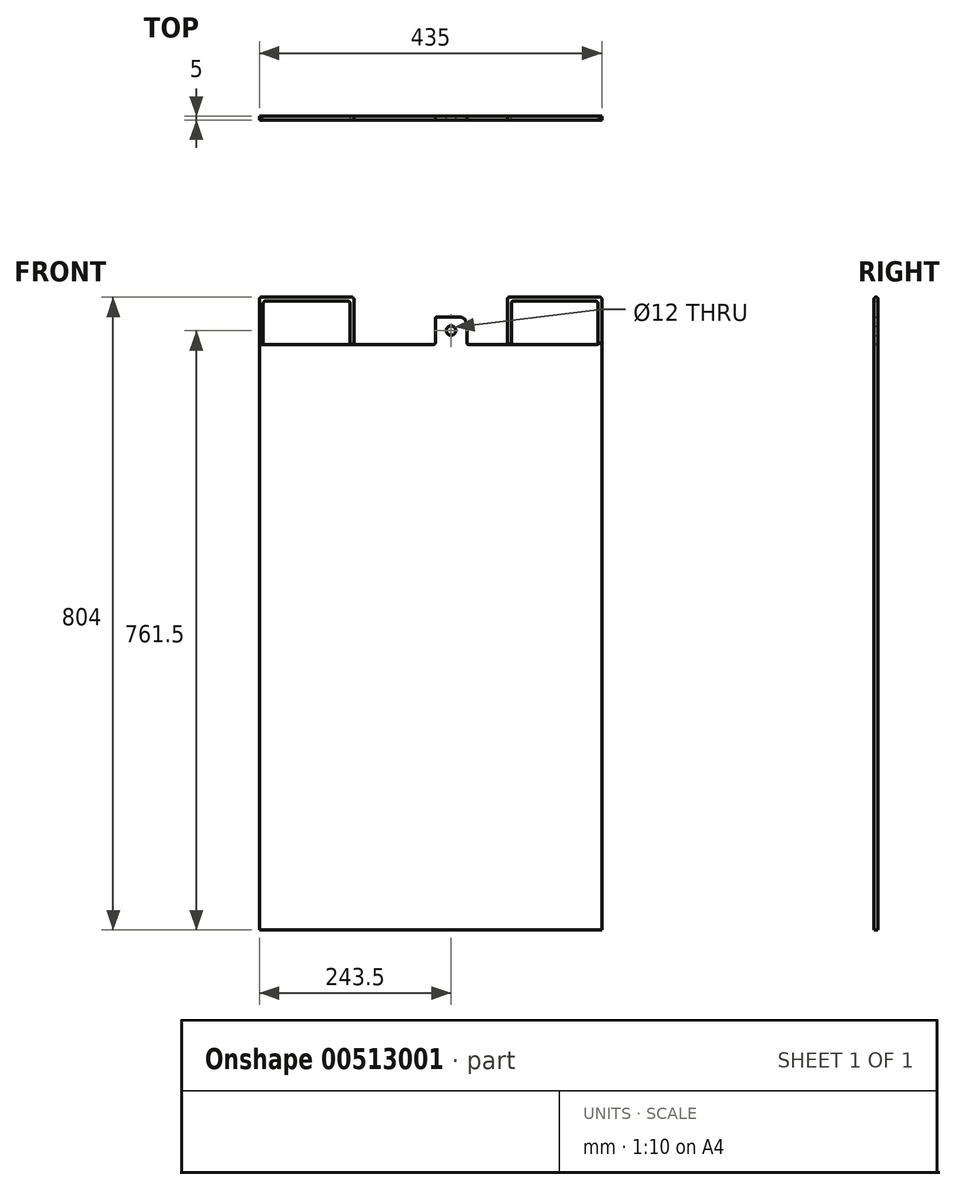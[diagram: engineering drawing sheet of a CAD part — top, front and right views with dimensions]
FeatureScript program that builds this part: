
annotation { "Feature Type Name" : "Feature", "Feature Type Description" : "" }
export const myFeature = defineFeature(function(context is Context, id is Id, definition is map)
    precondition{}
    {
        {
            var Q0;
            Q0=qCreatedBy(makeId("Front.planeOp"),FACE);
            var sketch = newSketch(context, id + "F0", { "sketchPlane" : qUnion([Q0])});
            skLineSegment(sketch, "E0.bottom", {"start": v(217.5, 372) * mm, "end": v(-217.5, 372) * mm});
            skLineSegment(sketch, "E0.top", {"start": v(217.5, -372) * mm, "end": v(-217.5, -372) * mm});
            skLineSegment(sketch, "E0.left", {"start": v(217.5, 372) * mm, "end": v(217.5, -372) * mm});
            skLineSegment(sketch, "E0.right", {"start": v(-217.5, 372) * mm, "end": v(-217.5, -372) * mm});
            skPoint(sketch, "E0.middle", {"position": v(0, 0) * mm});
            skLineSegment(sketch, "E1.bottom", {"start": v(6, 372) * mm, "end": v(46, 372) * mm});
            skLineSegment(sketch, "E1.top", {"start": v(6, 407) * mm, "end": v(46, 407) * mm});
            skLineSegment(sketch, "E1.left", {"start": v(6, 372) * mm, "end": v(6, 407) * mm});
            skLineSegment(sketch, "E1.right", {"start": v(46, 372) * mm, "end": v(46, 407) * mm});
            skPoint(sketch, "E2", {"position": v(0, 372) * mm});
            skLineSegment(sketch, "E3", {"start": v(0, -372) * mm, "end": v(0, 372) * mm, "construction": true});
            skLineSegment(sketch, "E4.bottom", {"start": v(-217.5, 372) * mm, "end": v(-97.5, 372) * mm});
            skLineSegment(sketch, "E4.top", {"start": v(-217.5, 432) * mm, "end": v(-97.5, 432) * mm});
            skLineSegment(sketch, "E4.left", {"start": v(-217.5, 372) * mm, "end": v(-217.5, 432) * mm});
            skLineSegment(sketch, "E4.right", {"start": v(-97.5, 372) * mm, "end": v(-97.5, 432) * mm});
            skPoint(sketch, "E5", {"position": v(26, 389.5) * mm});
            skPoint(sketch, "E5.positionSnap0", {"position": v(26, 372) * mm});
            skPoint(sketch, "E5.positionSnap1", {"position": v(46, 389.5) * mm});
            skLineSegment(sketch, "E6.0", {"start": v(-102.5, 372) * mm, "end": v(-102.5, 427) * mm});
            skLineSegment(sketch, "E6.1", {"start": v(-212.5, 427) * mm, "end": v(-102.5, 427) * mm});
            skLineSegment(sketch, "E6.2", {"start": v(-212.5, 372) * mm, "end": v(-212.5, 427) * mm});
            skLineSegment(sketch, "E7.MirrorCS", {"start": v(97.5, 372) * mm, "end": v(97.5, 432) * mm});
            skLineSegment(sketch, "E8.MirrorCS", {"start": v(102.5, 372) * mm, "end": v(102.5, 427) * mm});
            skLineSegment(sketch, "E9.MirrorCS", {"start": v(212.5, 427) * mm, "end": v(102.5, 427) * mm});
            skLineSegment(sketch, "E10.MirrorCS", {"start": v(217.5, 432) * mm, "end": v(97.5, 432) * mm});
            skLineSegment(sketch, "E11.MirrorCS", {"start": v(212.5, 372) * mm, "end": v(212.5, 427) * mm});
            skLineSegment(sketch, "E12.MirrorCS", {"start": v(217.5, 372) * mm, "end": v(217.5, 432) * mm});
            skSolve(sketch);
        }
        {
            var Q0;
            Q0 = qSketchRegion(id + "F0", true);
            extrude(context, id + "F1", {"entities" : qUnion([Q0]), "depth" : 5 * mm});
        }
        {
            var Q0;
            Q0=sQuery(id+"F0.wireOp",VERTEX,"E5");
            var Q1;
            Q1=makeQuery(id+"F1.opExtrude","SWEPT_BODY",BODY,{"disambiguationData":[OSD([sQuery(id+"F0.wireOp",EDGE,"E0.bottom"),sQuery(id+"F0.wireOp",EDGE,"E0.top"),sQuery(id+"F0.wireOp",EDGE,"E0.left"),sQuery(id+"F0.wireOp",EDGE,"E0.right"),sQuery(id+"F0.wireOp",EDGE,"E1.top"),sQuery(id+"F0.wireOp",EDGE,"E1.left"),sQuery(id+"F0.wireOp",EDGE,"E1.right"),sQuery(id+"F0.wireOp",EDGE,"E4.bottom"),sQuery(id+"F0.wireOp",EDGE,"E4.top"),sQuery(id+"F0.wireOp",EDGE,"E4.left"),sQuery(id+"F0.wireOp",EDGE,"E4.right"),sQuery(id+"F0.wireOp",EDGE,"E6.0"),sQuery(id+"F0.wireOp",EDGE,"E6.1"),sQuery(id+"F0.wireOp",EDGE,"E6.2"),sQuery(id+"F0.wireOp",EDGE,"E7.MirrorCS"),sQuery(id+"F0.wireOp",EDGE,"E8.MirrorCS"),sQuery(id+"F0.wireOp",EDGE,"E9.MirrorCS"),sQuery(id+"F0.wireOp",EDGE,"E10.MirrorCS"),sQuery(id+"F0.wireOp",EDGE,"E11.MirrorCS"),sQuery(id+"F0.wireOp",EDGE,"E12.MirrorCS")])]});
            hole(context, id + "F2", {"style" : HoleStyle.SIMPLE, "endStyle" : HoleEndStyle.THROUGH, "oppositeDirection" : true, "holeDiameter" : 12 * mm, "tappedDepth" : 12 * mm, "tapClearance" : 3, "locations" : qUnion([Q0]), "scope" : qUnion([Q1])});
        }
        {
            var Q0;
            Q0=makeQuery(id+"F1.opExtrude","SWEPT_EDGE",EDGE,{"disambiguationData":[OSD([sQuery(id+"F0.wireOp",EDGE,"E1.top"),sQuery(id+"F0.wireOp",EDGE,"E1.right")])]});
            fillet(context, id + "F3", {"entities" : qUnion([Q0]), "radius" : 10 * mm, "tangentPropagation" : true, "allowEdgeOverflow" : false});
        }
        {
            var Q0;
            Q0=makeQuery(id+"F1.opExtrude","CAP_EDGE",EDGE,{"disambiguationData":[OSD([sQuery(id+"F0.wireOp",EDGE,"E4.top")])],"isStart":true});
            var Q1;
            Q1=makeQuery(id+"F1.opExtrude","CAP_EDGE",EDGE,{"disambiguationData":[OSD([sQuery(id+"F0.wireOp",EDGE,"E4.top")])],"isStart":false});
            var Q2;
            Q2=makeQuery(id+"F1.opExtrude","CAP_EDGE",EDGE,{"disambiguationData":[OSD([sQuery(id+"F0.wireOp",EDGE,"E6.2")])],"isStart":false});
            var Q3;
            Q3=makeQuery(id+"F1.opExtrude","CAP_EDGE",EDGE,{"disambiguationData":[OSD([sQuery(id+"F0.wireOp",EDGE,"E6.2")])],"isStart":true});
            var Q4;
            Q4=makeQuery(id+"F1.opExtrude","CAP_EDGE",EDGE,{"disambiguationData":[OSD([sQuery(id+"F0.wireOp",EDGE,"E6.1")])],"isStart":false});
            var Q5;
            Q5=makeQuery(id+"F1.opExtrude","CAP_EDGE",EDGE,{"disambiguationData":[OSD([sQuery(id+"F0.wireOp",EDGE,"E6.1")])],"isStart":true});
            var Q6;
            Q6=makeQuery(id+"F1.opExtrude","CAP_EDGE",EDGE,{"disambiguationData":[OSD([sQuery(id+"F0.wireOp",EDGE,"E6.0")])],"isStart":false});
            var Q7;
            Q7=makeQuery(id+"F1.opExtrude","CAP_EDGE",EDGE,{"disambiguationData":[OSD([sQuery(id+"F0.wireOp",EDGE,"E6.0")])],"isStart":true});
            var Q8;
            Q8=makeQuery(id+"F1.opExtrude","CAP_EDGE",EDGE,{"disambiguationData":[OSD([sQuery(id+"F0.wireOp",EDGE,"E4.right")])],"isStart":false});
            var Q9;
            Q9=makeQuery(id+"F1.opExtrude","CAP_EDGE",EDGE,{"disambiguationData":[OSD([sQuery(id+"F0.wireOp",EDGE,"E4.right")])],"isStart":true});
            var Q10;
            Q10=makeQuery(id+"F1.opExtrude","SWEPT_EDGE",EDGE,{"disambiguationData":[OSD([sQuery(id+"F0.wireOp",EDGE,"E4.top"),sQuery(id+"F0.wireOp",EDGE,"E4.right")])]});
            var Q11;
            Q11=makeQuery(id+"F1.opExtrude","SWEPT_EDGE",EDGE,{"disambiguationData":[OSD([sQuery(id+"F0.wireOp",EDGE,"E4.top"),sQuery(id+"F0.wireOp",EDGE,"E4.left")])]});
            var Q12;
            Q12=makeQuery(id+"F1.opExtrude","SWEPT_EDGE",EDGE,{"disambiguationData":[OSD([sQuery(id+"F0.wireOp",EDGE,"E6.0"),sQuery(id+"F0.wireOp",EDGE,"E6.1")])]});
            var Q13;
            Q13=makeQuery(id+"F1.opExtrude","SWEPT_EDGE",EDGE,{"disambiguationData":[OSD([sQuery(id+"F0.wireOp",EDGE,"E6.1"),sQuery(id+"F0.wireOp",EDGE,"E6.2")])]});
            var Q14;
            Q14=makeQuery(id+"F1.opExtrude","CAP_EDGE",EDGE,{"disambiguationData":[OSD([sQuery(id+"F0.wireOp",EDGE,"E8.MirrorCS")])],"isStart":false});
            var Q15;
            Q15=makeQuery(id+"F1.opExtrude","CAP_EDGE",EDGE,{"disambiguationData":[OSD([sQuery(id+"F0.wireOp",EDGE,"E8.MirrorCS")])],"isStart":true});
            var Q16;
            Q16=makeQuery(id+"F1.opExtrude","CAP_EDGE",EDGE,{"disambiguationData":[OSD([sQuery(id+"F0.wireOp",EDGE,"E9.MirrorCS")])],"isStart":false});
            var Q17;
            Q17=makeQuery(id+"F1.opExtrude","CAP_EDGE",EDGE,{"disambiguationData":[OSD([sQuery(id+"F0.wireOp",EDGE,"E10.MirrorCS")])],"isStart":false});
            var Q18;
            Q18=makeQuery(id+"F1.opExtrude","CAP_EDGE",EDGE,{"disambiguationData":[OSD([sQuery(id+"F0.wireOp",EDGE,"E10.MirrorCS")])],"isStart":true});
            var Q19;
            Q19=makeQuery(id+"F1.opExtrude","CAP_EDGE",EDGE,{"disambiguationData":[OSD([sQuery(id+"F0.wireOp",EDGE,"E7.MirrorCS")])],"isStart":false});
            var Q20;
            Q20=makeQuery(id+"F1.opExtrude","CAP_EDGE",EDGE,{"disambiguationData":[OSD([sQuery(id+"F0.wireOp",EDGE,"E11.MirrorCS")])],"isStart":false});
            var Q21;
            Q21=makeQuery(id+"F1.opExtrude","CAP_EDGE",EDGE,{"disambiguationData":[OSD([sQuery(id+"F0.wireOp",EDGE,"E11.MirrorCS")])],"isStart":true});
            var Q22;
            Q22=makeQuery(id+"F1.opExtrude","CAP_EDGE",EDGE,{"disambiguationData":[OSD([sQuery(id+"F0.wireOp",EDGE,"E9.MirrorCS")])],"isStart":true});
            var Q23;
            Q23=makeQuery(id+"F1.opExtrude","SWEPT_EDGE",EDGE,{"disambiguationData":[OSD([sQuery(id+"F0.wireOp",EDGE,"E10.MirrorCS"),sQuery(id+"F0.wireOp",EDGE,"E12.MirrorCS")])]});
            var Q24;
            Q24=makeQuery(id+"F1.opExtrude","SWEPT_EDGE",EDGE,{"disambiguationData":[OSD([sQuery(id+"F0.wireOp",EDGE,"E7.MirrorCS"),sQuery(id+"F0.wireOp",EDGE,"E10.MirrorCS")])]});
            var Q25;
            Q25=makeQuery(id+"F1.opExtrude","CAP_EDGE",EDGE,{"disambiguationData":[OSD([sQuery(id+"F0.wireOp",EDGE,"E7.MirrorCS")])],"isStart":true});
            var Q26;
            Q26=makeQuery(id+"F1.opExtrude","SWEPT_EDGE",EDGE,{"disambiguationData":[OSD([sQuery(id+"F0.wireOp",EDGE,"E8.MirrorCS"),sQuery(id+"F0.wireOp",EDGE,"E9.MirrorCS")])]});
            var Q27;
            Q27=makeQuery(id+"F1.opExtrude","SWEPT_EDGE",EDGE,{"disambiguationData":[OSD([sQuery(id+"F0.wireOp",EDGE,"E9.MirrorCS"),sQuery(id+"F0.wireOp",EDGE,"E11.MirrorCS")])]});
            fillet(context, id + "F4", {"entities" : qUnion([Q0, Q1, Q2, Q3, Q4, Q5, Q6, Q7, Q8, Q9, Q10, Q11, Q12, Q13, Q14, Q15, Q16, Q17, Q18, Q19, Q20, Q21, Q22, Q23, Q24, Q25, Q26, Q27]), "radius" : 2.5 * mm, "tangentPropagation" : true, "allowEdgeOverflow" : false});
        }
        {
            var Q0;
            {var subQ0=sQuery(id+"F0.wireOp",EDGE,"E4.right");var subQ1=sQuery(id+"F0.wireOp",EDGE,"E0.bottom");Q0=makeQuery(id+"F4.opFillet","BLEND_EDGE",EDGE,{"blendedFrom":[makeQuery(id+"F1.opExtrude","CAP_EDGE",EDGE,{"disambiguationData":[OSD([subQ0])],"isStart":true}),makeQuery(id+"F1.opExtrude","SWEPT_FACE",FACE,{"disambiguationData":[OSD([subQ1]),TDD([makeQuery(id+"F0.imprint","IMPRINT",EDGE,{"disambiguationData":[TD([[makeQuery(id+"F0.imprint","INTERSECT",VERTEX,{"derivedFrom":[subQ1,sQuery(id+"F0.wireOp",EDGE,"E4.bottom"),subQ0]}),1.0]])],"derivedFrom":subQ1})])]})],"blendedInto":[makeQuery(id+"F1.opExtrude","SWEPT_FACE",FACE,{"disambiguationData":[OSD([subQ1]),TDD([makeQuery(id+"F0.imprint","IMPRINT",EDGE,{"disambiguationData":[TD([[makeQuery(id+"F0.imprint","INTERSECT",VERTEX,{"derivedFrom":[subQ1,sQuery(id+"F0.wireOp",EDGE,"E4.bottom"),subQ0]}),1.0]])],"derivedFrom":subQ1})])]})]});}
            var Q1;
            Q1=makeQuery(id+"F4.opFillet","BLEND_EDGE",EDGE,{"blendedFrom":[makeQuery(id+"F1.opExtrude","CAP_EDGE",EDGE,{"disambiguationData":[OSD([sQuery(id+"F0.wireOp",EDGE,"E6.2")])],"isStart":true}),makeQuery(id+"F1.opExtrude","SWEPT_FACE",FACE,{"disambiguationData":[OSD([sQuery(id+"F0.wireOp",EDGE,"E4.bottom")])]})],"blendedInto":[makeQuery(id+"F1.opExtrude","SWEPT_FACE",FACE,{"disambiguationData":[OSD([sQuery(id+"F0.wireOp",EDGE,"E4.bottom")])]})]});
            var Q2;
            {var subQ0=sQuery(id+"F0.wireOp",EDGE,"E0.bottom");var subQ1=sQuery(id+"F0.wireOp",EDGE,"E11.MirrorCS");Q2=makeQuery(id+"F4.opFillet","BLEND_EDGE",EDGE,{"blendedFrom":[makeQuery(id+"F1.opExtrude","CAP_EDGE",EDGE,{"disambiguationData":[OSD([subQ1])],"isStart":true}),makeQuery(id+"F1.opExtrude","SWEPT_FACE",FACE,{"disambiguationData":[OSD([subQ0]),TDD([makeQuery(id+"F0.imprint","IMPRINT",EDGE,{"disambiguationData":[TD([[makeQuery(id+"F0.imprint","INTERSECT",VERTEX,{"derivedFrom":[subQ0,sQuery(id+"F0.wireOp",EDGE,"E8.MirrorCS")]}),1.0]])],"derivedFrom":subQ0})])]})],"blendedInto":[makeQuery(id+"F1.opExtrude","SWEPT_FACE",FACE,{"disambiguationData":[OSD([subQ0]),TDD([makeQuery(id+"F0.imprint","IMPRINT",EDGE,{"disambiguationData":[TD([[makeQuery(id+"F0.imprint","INTERSECT",VERTEX,{"derivedFrom":[subQ0,sQuery(id+"F0.wireOp",EDGE,"E8.MirrorCS")]}),1.0]])],"derivedFrom":subQ0})])]})]});}
            var Q3;
            {var subQ0=sQuery(id+"F0.wireOp",EDGE,"E8.MirrorCS");var subQ1=sQuery(id+"F0.wireOp",EDGE,"E0.bottom");Q3=makeQuery(id+"F4.opFillet","BLEND_EDGE",EDGE,{"blendedFrom":[makeQuery(id+"F1.opExtrude","CAP_EDGE",EDGE,{"disambiguationData":[OSD([subQ0])],"isStart":true}),makeQuery(id+"F1.opExtrude","SWEPT_FACE",FACE,{"disambiguationData":[OSD([subQ1]),TDD([makeQuery(id+"F0.imprint","IMPRINT",EDGE,{"disambiguationData":[TD([[makeQuery(id+"F0.imprint","INTERSECT",VERTEX,{"derivedFrom":[subQ1,subQ0]}),1.0]])],"derivedFrom":subQ1})])]})],"blendedInto":[makeQuery(id+"F1.opExtrude","SWEPT_FACE",FACE,{"disambiguationData":[OSD([subQ1]),TDD([makeQuery(id+"F0.imprint","IMPRINT",EDGE,{"disambiguationData":[TD([[makeQuery(id+"F0.imprint","INTERSECT",VERTEX,{"derivedFrom":[subQ1,subQ0]}),1.0]])],"derivedFrom":subQ1})])]})]});}
            var Q4;
            Q4=makeQuery(id+"F1.opExtrude","SWEPT_EDGE",EDGE,{"disambiguationData":[OSD([sQuery(id+"F0.wireOp",EDGE,"E0.bottom"),sQuery(id+"F0.wireOp",EDGE,"E1.bottom"),sQuery(id+"F0.wireOp",EDGE,"E1.left")])]});
            var Q5;
            Q5=makeQuery(id+"F1.opExtrude","SWEPT_EDGE",EDGE,{"disambiguationData":[OSD([sQuery(id+"F0.wireOp",EDGE,"E0.bottom"),sQuery(id+"F0.wireOp",EDGE,"E1.bottom"),sQuery(id+"F0.wireOp",EDGE,"E1.right")])]});
            var Q6;
            Q6=makeQuery(id+"F1.opExtrude","SWEPT_EDGE",EDGE,{"disambiguationData":[OSD([sQuery(id+"F0.wireOp",EDGE,"E1.top"),sQuery(id+"F0.wireOp",EDGE,"E1.left")])]});
            fillet(context, id + "F5", {"entities" : qUnion([Q0, Q1, Q2, Q3, Q4, Q5, Q6]), "radius" : 2 * mm, "tangentPropagation" : true, "allowEdgeOverflow" : false});
        }
    });
